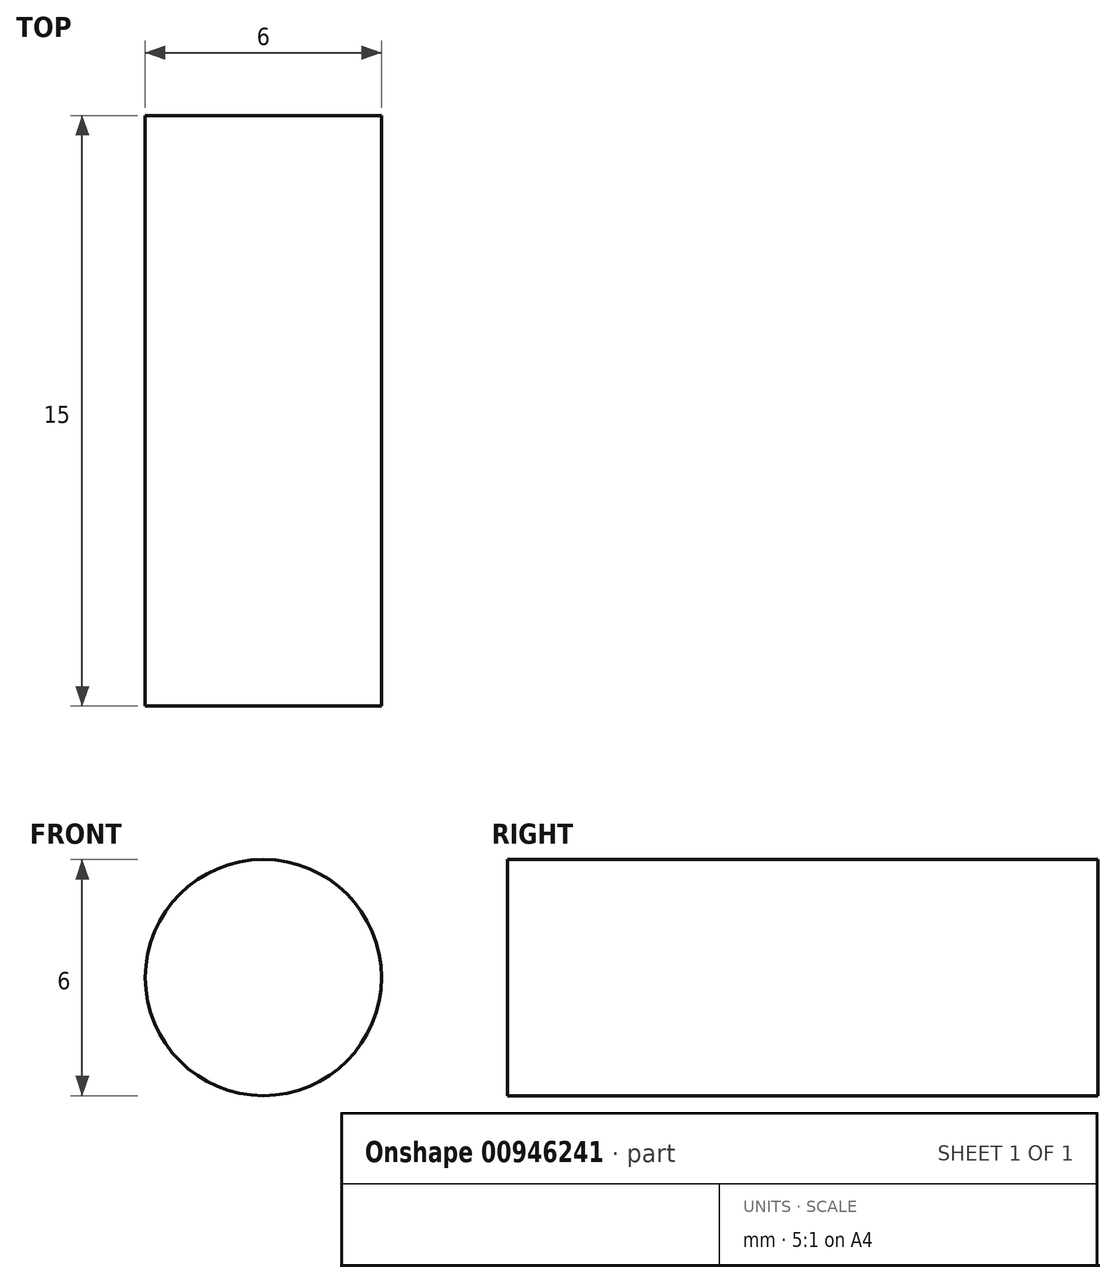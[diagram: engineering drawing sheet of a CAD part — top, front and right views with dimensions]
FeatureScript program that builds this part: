
annotation { "Feature Type Name" : "Feature", "Feature Type Description" : "" }
export const myFeature = defineFeature(function(context is Context, id is Id, definition is map)
    precondition{}
    {
        {
            var Q0;
            Q0=qCreatedBy(makeId("Front.planeOp"),FACE);
            var sketch = newSketch(context, id + "F0", { "sketchPlane" : qUnion([Q0])});
            skCircle(sketch, "E0", {"center": v(0, 0) * mm, "radius": 3 * mm});
            skSolve(sketch);
        }
        {
            var Q0;
            Q0=makeQuery(id+"F0.imprint","IMPRINT",FACE,{"disambiguationData":[TD([[makeQuery(id+"F0.imprint","IMPRINT",EDGE,{"derivedFrom":sQuery(id+"F0.wireOp",EDGE,"E0")}),1.0]])]});
            extrude(context, id + "F1", {"entities" : qUnion([Q0]), "depth" : 15 * mm, "offsetDistance" : 25.4 * mm});
        }
    });
